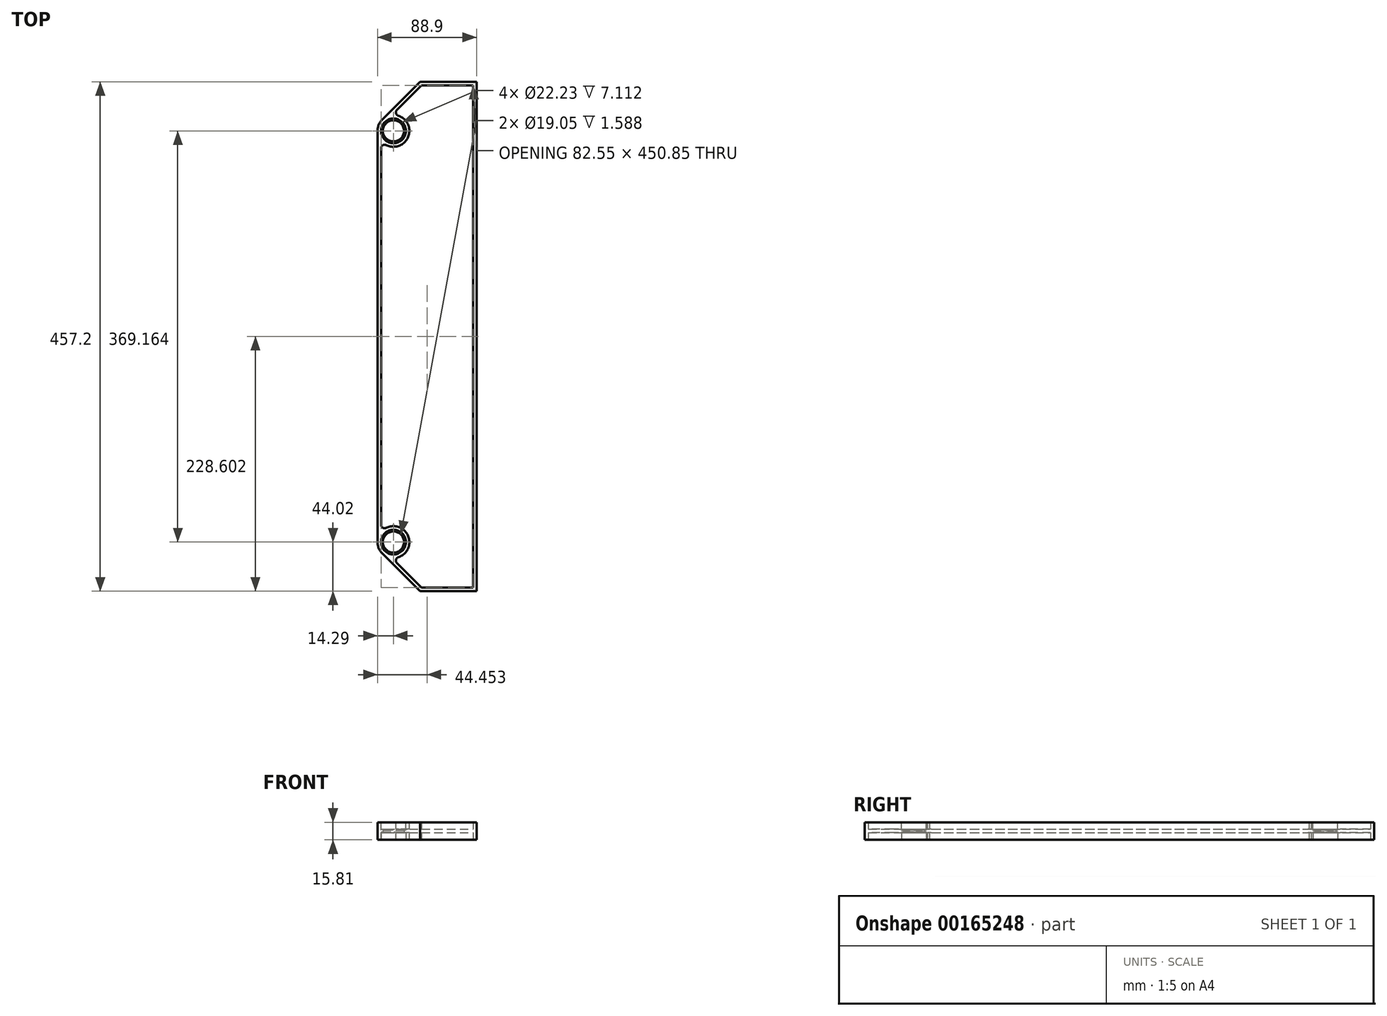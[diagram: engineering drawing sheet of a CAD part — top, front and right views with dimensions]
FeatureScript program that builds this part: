
annotation { "Feature Type Name" : "Feature", "Feature Type Description" : "" }
export const myFeature = defineFeature(function(context is Context, id is Id, definition is map)
    precondition{}
    {
        {
            var Q0;
            Q0=qCreatedBy(makeId("Top.planeOp"),FACE);
            var sketch = newSketch(context, id + "F0", { "sketchPlane" : qUnion([Q0])});
            skCircle(sketch, "E0", {"center": v(0, 0) * mm, "radius": 9.53 * mm});
            skArc(sketch, "E1", {"start": v(-14.29, 0) * mm, "mid": v(-13.2, -5.47) * mm, "end": v(-10.1, -10.1) * mm});
            skLineSegment(sketch, "E2", {"start": v(-14.29, 0) * mm, "end": v(-14.29, 369.16) * mm});
            skArc(sketch, "E3", {"start": v(-10.1, 379.27) * mm, "mid": v(-13.2, 374.63) * mm, "end": v(-14.29, 369.16) * mm});
            skCircle(sketch, "E4", {"center": v(0, 369.16) * mm, "radius": 9.53 * mm});
            skLineSegment(sketch, "E5", {"start": v(-10.1, -10.1) * mm, "end": v(23.81, -44.02) * mm});
            skLineSegment(sketch, "E6", {"start": v(23.81, -44.02) * mm, "end": v(74.61, -44.02) * mm});
            skLineSegment(sketch, "E7", {"start": v(74.61, -44.02) * mm, "end": v(74.61, 413.18) * mm});
            skLineSegment(sketch, "E8", {"start": v(74.61, 413.18) * mm, "end": v(23.81, 413.18) * mm});
            skLineSegment(sketch, "E9", {"start": v(23.81, 413.18) * mm, "end": v(-10.1, 379.27) * mm});
            skLineSegment(sketch, "E10", {"start": v(-14.29, 184.58) * mm, "end": v(23.81, 184.58) * mm, "construction": true});
            skLineSegment(sketch, "E11", {"start": v(23.81, -44.02) * mm, "end": v(23.81, 413.18) * mm, "construction": true});
            skSolve(sketch);
        }
        {
            var Q0;
            Q0=qSketchRegion(id+"F0",true);
            extrude(context, id + "F1", {"entities" : qUnion([Q0]), "depth" : 15.8 * mm});
        }
        {
            var Q0;
            Q0=makeQuery(id+"F1.opExtrude","CAP_FACE",FACE,{"disambiguationData":[OSD([sQuery(id+"F0.wireOp",EDGE,"E0"),sQuery(id+"F0.wireOp",EDGE,"E1"),sQuery(id+"F0.wireOp",EDGE,"E2"),sQuery(id+"F0.wireOp",EDGE,"E3"),sQuery(id+"F0.wireOp",EDGE,"E4"),sQuery(id+"F0.wireOp",EDGE,"E5"),sQuery(id+"F0.wireOp",EDGE,"E6"),sQuery(id+"F0.wireOp",EDGE,"E7"),sQuery(id+"F0.wireOp",EDGE,"E8"),sQuery(id+"F0.wireOp",EDGE,"E9")])],"isStart":false});
            var sketch = newSketch(context, id + "F2", { "sketchPlane" : qUnion([Q0])});
            skCircle(sketch, "E12", {"center": v(0, 369.16) * mm, "radius": 11.11 * mm});
            skCircle(sketch, "E13", {"center": v(0, 0) * mm, "radius": 11.11 * mm});
            skSolve(sketch);
        }
        {
            var Q0;
            Q0=qSketchRegion(id+"F2",true);
            extrude(context, id + "F3", {"entities" : qUnion([Q0]), "operationType" : NewBodyOperationType.REMOVE, "oppositeDirection" : true, "depth" : 7.11 * mm});
        }
        {
            var Q0;
            Q0=makeQuery(id+"F1.opExtrude","CAP_FACE",FACE,{"disambiguationData":[OSD([sQuery(id+"F0.wireOp",EDGE,"E0"),sQuery(id+"F0.wireOp",EDGE,"E1"),sQuery(id+"F0.wireOp",EDGE,"E2"),sQuery(id+"F0.wireOp",EDGE,"E3"),sQuery(id+"F0.wireOp",EDGE,"E4"),sQuery(id+"F0.wireOp",EDGE,"E5"),sQuery(id+"F0.wireOp",EDGE,"E6"),sQuery(id+"F0.wireOp",EDGE,"E7"),sQuery(id+"F0.wireOp",EDGE,"E8"),sQuery(id+"F0.wireOp",EDGE,"E9")])],"isStart":true});
            var sketch = newSketch(context, id + "F4", { "sketchPlane" : qUnion([Q0])});
            skCircle(sketch, "E14", {"center": v(0, 0) * mm, "radius": 11.11 * mm});
            skCircle(sketch, "E15", {"center": v(0, -369.16) * mm, "radius": 11.11 * mm});
            skSolve(sketch);
        }
        {
            var Q0;
            Q0=qSketchRegion(id+"F4",true);
            extrude(context, id + "F5", {"entities" : qUnion([Q0]), "operationType" : NewBodyOperationType.REMOVE, "oppositeDirection" : true, "depth" : 7.11 * mm});
        }
        {
            var Q0;
            Q0=makeQuery(id+"F1.opExtrude","CAP_FACE",FACE,{"disambiguationData":[OSD([sQuery(id+"F0.wireOp",EDGE,"E0"),sQuery(id+"F0.wireOp",EDGE,"E1"),sQuery(id+"F0.wireOp",EDGE,"E2"),sQuery(id+"F0.wireOp",EDGE,"E3"),sQuery(id+"F0.wireOp",EDGE,"E4"),sQuery(id+"F0.wireOp",EDGE,"E5"),sQuery(id+"F0.wireOp",EDGE,"E6"),sQuery(id+"F0.wireOp",EDGE,"E7"),sQuery(id+"F0.wireOp",EDGE,"E8"),sQuery(id+"F0.wireOp",EDGE,"E9")])],"isStart":true});
            shell(context, id + "F6", {"entities" : qUnion([Q0]), "thickness" : 3.17 * mm});
        }
        {
            var Q0;
            {var subQ0=sQuery(id+"F4.wireOp",EDGE,"E15");var subQ1=sQuery(id+"F2.wireOp",EDGE,"E12");var subQ2=sQuery(id+"F0.wireOp",EDGE,"E9");var subQ3=sQuery(id+"F0.wireOp",EDGE,"E8");var subQ4=sQuery(id+"F0.wireOp",EDGE,"E7");var subQ5=sQuery(id+"F0.wireOp",EDGE,"E6");var subQ6=sQuery(id+"F0.wireOp",EDGE,"E5");var subQ7=sQuery(id+"F0.wireOp",EDGE,"E4");var subQ8=sQuery(id+"F0.wireOp",EDGE,"E3");var subQ9=sQuery(id+"F0.wireOp",EDGE,"E2");var subQ10=sQuery(id+"F0.wireOp",EDGE,"E1");var subQ11=sQuery(id+"F0.wireOp",EDGE,"E0");var subQ12=makeQuery(id+"F1.opExtrude","CAP_FACE",FACE,{"disambiguationData":[OSD([subQ11,subQ10,subQ9,subQ8,subQ7,subQ6,subQ5,subQ4,subQ3,subQ2])],"isStart":false});var subQ13=makeQuery(id+"F5.boolean.opBoolean","COPY",FACE,{"derivedFrom":makeQuery(id+"F5.opExtrude","SWEPT_FACE",FACE,{"disambiguationData":[OSD([subQ0])]})});var subQ14=makeQuery(id+"F3.boolean.opBoolean","COPY",FACE,{"derivedFrom":makeQuery(id+"F3.opExtrude","SWEPT_FACE",FACE,{"disambiguationData":[OSD([subQ1])]})});var subQ15=makeQuery(id+"F1.opExtrude","SWEPT_FACE",FACE,{"disambiguationData":[OSD([subQ2])]});Q0=makeQuery(id+"F11.boolean.opBoolean","SPLIT",EDGE,{"disambiguationData":[TD([subQ12])],"derivedFrom":makeQuery(id+"F8.boolean.opBoolean","MERGE",EDGE,{"derivedFrom":[makeQuery(id+"F6.opShell","TWEAK_EDGE",EDGE,{"derivedFrom":[subQ15,subQ14,subQ13]}),makeQuery(id+"F8.opExtrude","SWEPT_EDGE",EDGE,{"disambiguationData":[OSD([subQ11,subQ10,subQ9,subQ8,subQ7,subQ6,subQ5,subQ4,subQ3,subQ2,subQ1,subQ0]),TDD([makeQuery(id+"F6.opShell","TWEAK_VERTEX",VERTEX,{"derivedFrom":[subQ15,subQ14,subQ12,subQ13]})])]})]})});}
            var Q1;
            {var subQ0=sQuery(id+"F4.wireOp",EDGE,"E15");var subQ1=sQuery(id+"F2.wireOp",EDGE,"E12");var subQ2=sQuery(id+"F0.wireOp",EDGE,"E2");var subQ3=sQuery(id+"F0.wireOp",EDGE,"E9");var subQ4=sQuery(id+"F0.wireOp",EDGE,"E8");var subQ5=sQuery(id+"F0.wireOp",EDGE,"E7");var subQ6=sQuery(id+"F0.wireOp",EDGE,"E6");var subQ7=sQuery(id+"F0.wireOp",EDGE,"E5");var subQ8=sQuery(id+"F0.wireOp",EDGE,"E4");var subQ9=sQuery(id+"F0.wireOp",EDGE,"E3");var subQ10=sQuery(id+"F0.wireOp",EDGE,"E1");var subQ11=sQuery(id+"F0.wireOp",EDGE,"E0");var subQ12=makeQuery(id+"F1.opExtrude","CAP_FACE",FACE,{"disambiguationData":[OSD([subQ11,subQ10,subQ2,subQ9,subQ8,subQ7,subQ6,subQ5,subQ4,subQ3])],"isStart":false});var subQ13=makeQuery(id+"F5.boolean.opBoolean","COPY",FACE,{"derivedFrom":makeQuery(id+"F5.opExtrude","SWEPT_FACE",FACE,{"disambiguationData":[OSD([subQ0])]})});var subQ14=makeQuery(id+"F3.boolean.opBoolean","COPY",FACE,{"derivedFrom":makeQuery(id+"F3.opExtrude","SWEPT_FACE",FACE,{"disambiguationData":[OSD([subQ1])]})});var subQ15=makeQuery(id+"F1.opExtrude","SWEPT_FACE",FACE,{"disambiguationData":[OSD([subQ2])]});Q1=makeQuery(id+"F11.boolean.opBoolean","SPLIT",EDGE,{"disambiguationData":[TD([subQ12])],"derivedFrom":makeQuery(id+"F8.boolean.opBoolean","MERGE",EDGE,{"derivedFrom":[makeQuery(id+"F6.opShell","TWEAK_EDGE",EDGE,{"derivedFrom":[subQ15,subQ14,subQ13]}),makeQuery(id+"F8.opExtrude","SWEPT_EDGE",EDGE,{"disambiguationData":[OSD([subQ11,subQ10,subQ2,subQ9,subQ8,subQ7,subQ6,subQ5,subQ4,subQ3,subQ1,subQ0]),TDD([makeQuery(id+"F6.opShell","TWEAK_VERTEX",VERTEX,{"derivedFrom":[subQ15,subQ14,subQ12,subQ13]})])]})]})});}
            var Q2;
            {var subQ0=sQuery(id+"F4.wireOp",EDGE,"E14");var subQ1=sQuery(id+"F2.wireOp",EDGE,"E13");var subQ2=sQuery(id+"F0.wireOp",EDGE,"E9");var subQ3=sQuery(id+"F0.wireOp",EDGE,"E8");var subQ4=sQuery(id+"F0.wireOp",EDGE,"E7");var subQ5=sQuery(id+"F0.wireOp",EDGE,"E6");var subQ6=sQuery(id+"F0.wireOp",EDGE,"E5");var subQ7=sQuery(id+"F0.wireOp",EDGE,"E4");var subQ8=sQuery(id+"F0.wireOp",EDGE,"E3");var subQ9=sQuery(id+"F0.wireOp",EDGE,"E2");var subQ10=sQuery(id+"F0.wireOp",EDGE,"E1");var subQ11=sQuery(id+"F0.wireOp",EDGE,"E0");var subQ12=makeQuery(id+"F1.opExtrude","CAP_FACE",FACE,{"disambiguationData":[OSD([subQ11,subQ10,subQ9,subQ8,subQ7,subQ6,subQ5,subQ4,subQ3,subQ2])],"isStart":false});var subQ13=makeQuery(id+"F5.boolean.opBoolean","COPY",FACE,{"derivedFrom":makeQuery(id+"F5.opExtrude","SWEPT_FACE",FACE,{"disambiguationData":[OSD([subQ0])]})});var subQ14=makeQuery(id+"F3.boolean.opBoolean","COPY",FACE,{"derivedFrom":makeQuery(id+"F3.opExtrude","SWEPT_FACE",FACE,{"disambiguationData":[OSD([subQ1])]})});var subQ15=makeQuery(id+"F1.opExtrude","SWEPT_FACE",FACE,{"disambiguationData":[OSD([subQ6])]});Q2=makeQuery(id+"F11.boolean.opBoolean","SPLIT",EDGE,{"disambiguationData":[TD([subQ12])],"derivedFrom":makeQuery(id+"F8.boolean.opBoolean","MERGE",EDGE,{"derivedFrom":[makeQuery(id+"F6.opShell","TWEAK_EDGE",EDGE,{"derivedFrom":[subQ15,subQ14,subQ13]}),makeQuery(id+"F8.opExtrude","SWEPT_EDGE",EDGE,{"disambiguationData":[OSD([subQ11,subQ10,subQ9,subQ8,subQ7,subQ6,subQ5,subQ4,subQ3,subQ2,subQ1,subQ0]),TDD([makeQuery(id+"F6.opShell","TWEAK_VERTEX",VERTEX,{"derivedFrom":[subQ15,subQ14,subQ12,subQ13]})])]})]})});}
            var Q3;
            {var subQ0=sQuery(id+"F4.wireOp",EDGE,"E14");var subQ1=sQuery(id+"F2.wireOp",EDGE,"E13");var subQ2=sQuery(id+"F0.wireOp",EDGE,"E9");var subQ3=sQuery(id+"F0.wireOp",EDGE,"E8");var subQ4=sQuery(id+"F0.wireOp",EDGE,"E7");var subQ5=sQuery(id+"F0.wireOp",EDGE,"E6");var subQ6=sQuery(id+"F0.wireOp",EDGE,"E5");var subQ7=sQuery(id+"F0.wireOp",EDGE,"E4");var subQ8=sQuery(id+"F0.wireOp",EDGE,"E3");var subQ9=sQuery(id+"F0.wireOp",EDGE,"E2");var subQ10=sQuery(id+"F0.wireOp",EDGE,"E1");var subQ11=sQuery(id+"F0.wireOp",EDGE,"E0");var subQ12=makeQuery(id+"F1.opExtrude","CAP_FACE",FACE,{"disambiguationData":[OSD([subQ11,subQ10,subQ9,subQ8,subQ7,subQ6,subQ5,subQ4,subQ3,subQ2])],"isStart":false});var subQ13=makeQuery(id+"F5.boolean.opBoolean","COPY",FACE,{"derivedFrom":makeQuery(id+"F5.opExtrude","SWEPT_FACE",FACE,{"disambiguationData":[OSD([subQ0])]})});var subQ14=makeQuery(id+"F3.boolean.opBoolean","COPY",FACE,{"derivedFrom":makeQuery(id+"F3.opExtrude","SWEPT_FACE",FACE,{"disambiguationData":[OSD([subQ1])]})});var subQ15=makeQuery(id+"F1.opExtrude","SWEPT_FACE",FACE,{"disambiguationData":[OSD([subQ9])]});Q3=makeQuery(id+"F11.boolean.opBoolean","SPLIT",EDGE,{"disambiguationData":[TD([subQ12])],"derivedFrom":makeQuery(id+"F8.boolean.opBoolean","MERGE",EDGE,{"derivedFrom":[makeQuery(id+"F6.opShell","TWEAK_EDGE",EDGE,{"derivedFrom":[subQ15,subQ14,subQ13]}),makeQuery(id+"F8.opExtrude","SWEPT_EDGE",EDGE,{"disambiguationData":[OSD([subQ11,subQ10,subQ9,subQ8,subQ7,subQ6,subQ5,subQ4,subQ3,subQ2,subQ1,subQ0]),TDD([makeQuery(id+"F6.opShell","TWEAK_VERTEX",VERTEX,{"derivedFrom":[subQ15,subQ14,subQ12,subQ13]})])]})]})});}
            fillet(context, id + "F7", {"entities" : qUnion([Q0, Q1, Q2, Q3]), "radius" : 3.17 * mm, "tangentPropagation" : true, "allowEdgeOverflow" : false});
        }
        {
            var Q0;
            Q0=makeQuery(id+"F6.opShell","OFFSET_FACE",FACE,{"disambiguationData":[OSD([sQuery(id+"F0.wireOp",EDGE,"E0"),sQuery(id+"F0.wireOp",EDGE,"E1"),sQuery(id+"F0.wireOp",EDGE,"E2"),sQuery(id+"F0.wireOp",EDGE,"E3"),sQuery(id+"F0.wireOp",EDGE,"E4"),sQuery(id+"F0.wireOp",EDGE,"E5"),sQuery(id+"F0.wireOp",EDGE,"E6"),sQuery(id+"F0.wireOp",EDGE,"E7"),sQuery(id+"F0.wireOp",EDGE,"E8"),sQuery(id+"F0.wireOp",EDGE,"E9")])]});
            var Q1;
            Q1=makeQuery(id+"F1.opExtrude","CAP_FACE",FACE,{"disambiguationData":[OSD([sQuery(id+"F0.wireOp",EDGE,"E0"),sQuery(id+"F0.wireOp",EDGE,"E1"),sQuery(id+"F0.wireOp",EDGE,"E2"),sQuery(id+"F0.wireOp",EDGE,"E3"),sQuery(id+"F0.wireOp",EDGE,"E4"),sQuery(id+"F0.wireOp",EDGE,"E5"),sQuery(id+"F0.wireOp",EDGE,"E6"),sQuery(id+"F0.wireOp",EDGE,"E7"),sQuery(id+"F0.wireOp",EDGE,"E8"),sQuery(id+"F0.wireOp",EDGE,"E9")])],"isStart":false});
            extrude(context, id + "F8", {"entities" : qUnion([Q0]), "operationType" : NewBodyOperationType.REMOVE, "endBound" : BoundingType.UP_TO_SURFACE, "oppositeDirection" : true, "endBoundEntityFace" : qUnion([Q1]), "depth" : 25.4 * mm});
        }
        {
            var Q0;
            Q0=makeQuery(id+"F1.opExtrude","CAP_FACE",FACE,{"disambiguationData":[OSD([sQuery(id+"F0.wireOp",EDGE,"E0"),sQuery(id+"F0.wireOp",EDGE,"E1"),sQuery(id+"F0.wireOp",EDGE,"E2"),sQuery(id+"F0.wireOp",EDGE,"E3"),sQuery(id+"F0.wireOp",EDGE,"E4"),sQuery(id+"F0.wireOp",EDGE,"E5"),sQuery(id+"F0.wireOp",EDGE,"E6"),sQuery(id+"F0.wireOp",EDGE,"E7"),sQuery(id+"F0.wireOp",EDGE,"E8"),sQuery(id+"F0.wireOp",EDGE,"E9")])],"isStart":false});
            cPlane(context, id + "F9", {"entities" : qUnion([Q0]), "cplaneType" : CPlaneType.OFFSET, "offset" : 7.9 * mm, "oppositeDirection" : true, "width" : 152.4 * mm, "height" : 152.4 * mm});
        }
        {
            var Q0;
            Q0=qCreatedBy(id+"F9.planeOp",FACE);
            var sketch = newSketch(context, id + "F10", { "sketchPlane" : qUnion([Q0])});
            skLineSegment(sketch, "E16.bottom", {"start": v(74.61, 413.18) * mm, "end": v(-14.29, 413.18) * mm});
            skLineSegment(sketch, "E16.top", {"start": v(74.61, -44.02) * mm, "end": v(-14.29, -44.02) * mm});
            skLineSegment(sketch, "E16.left", {"start": v(74.61, 413.18) * mm, "end": v(74.61, -44.02) * mm});
            skLineSegment(sketch, "E16.right", {"start": v(-14.29, 413.18) * mm, "end": v(-14.29, -44.02) * mm});
            skCircle(sketch, "E17", {"center": v(0, 0) * mm, "radius": 11.11 * mm});
            skCircle(sketch, "E18", {"center": v(0, 369.16) * mm, "radius": 11.11 * mm});
            skLineSegment(sketch, "E19", {"start": v(-10.1, 379.27) * mm, "end": v(23.81, 413.18) * mm});
            skArc(sketch, "E20", {"start": v(-10.1, 379.27) * mm, "mid": v(-13.2, 374.63) * mm, "end": v(-14.29, 369.16) * mm});
            skLineSegment(sketch, "E21", {"start": v(23.81, -44.02) * mm, "end": v(-10.1, -10.1) * mm});
            skArc(sketch, "E22", {"start": v(-14.29, 0) * mm, "mid": v(-13.2, -5.47) * mm, "end": v(-10.1, -10.1) * mm});
            skSolve(sketch);
        }
        {
            var Q0;
            {var subQ3=sQuery(id+"F10.wireOp",EDGE,"E16.left");Q0=makeQuery(id+"F10.imprint","IMPRINT",FACE,{"disambiguationData":[TD([[makeQuery(id+"F10.imprint","IMPRINT",EDGE,{"derivedFrom":subQ3}),-1.0]])]});}
            extrude(context, id + "F11", {"entities" : qUnion([Q0]), "operationType" : NewBodyOperationType.ADD, "endBound" : BoundingType.SYMMETRIC, "depth" : 3.17 * mm});
        }
    });
